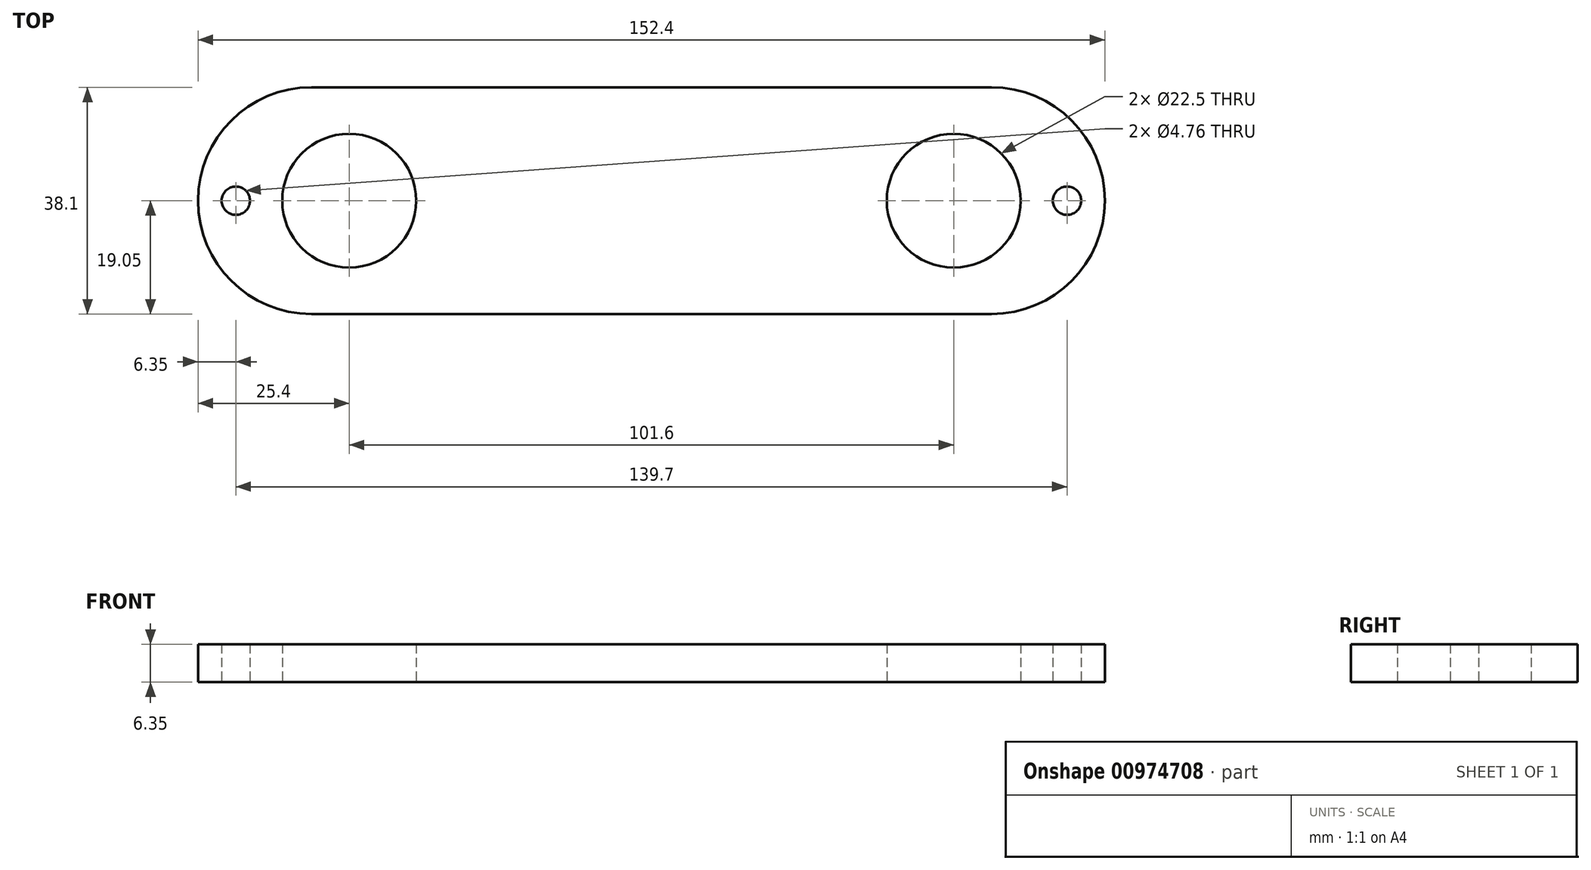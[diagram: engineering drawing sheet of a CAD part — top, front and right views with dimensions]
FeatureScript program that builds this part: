
annotation { "Feature Type Name" : "Feature", "Feature Type Description" : "" }
export const myFeature = defineFeature(function(context is Context, id is Id, definition is map)
    precondition{}
    {
        {
            var Q0;
            Q0=qCreatedBy(makeId("Top.planeOp"),FACE);
            var sketch = newSketch(context, id + "F0", { "sketchPlane" : qUnion([Q0])});
            skArc(sketch, "E0", {"start": v(-57.15, 19.05) * mm, "mid": v(-76.2, 0) * mm, "end": v(-57.15, -19.05) * mm});
            skLineSegment(sketch, "E1", {"start": v(-57.15, 19.05) * mm, "end": v(57.15, 19.05) * mm});
            skLineSegment(sketch, "E2", {"start": v(-57.15, -19.05) * mm, "end": v(57.15, -19.05) * mm});
            skArc(sketch, "E3", {"start": v(57.15, -19.05) * mm, "mid": v(76.2, 0) * mm, "end": v(57.15, 19.05) * mm});
            skCircle(sketch, "E4", {"center": v(-50.8, 0) * mm, "radius": 11.25 * mm});
            skCircle(sketch, "E5", {"center": v(50.8, 0) * mm, "radius": 11.25 * mm});
            skPoint(sketch, "E6", {"position": v(0, 0) * mm});
            skSolve(sketch);
        }
        {
            var Q0;
            Q0=makeQuery(id+"F0.imprint","IMPRINT",FACE,{"disambiguationData":[TD([[makeQuery(id+"F0.imprint","IMPRINT",EDGE,{"derivedFrom":sQuery(id+"F0.wireOp",EDGE,"E0")}),1.0]])]});
            var sketch = newSketch(context, id + "F1", { "sketchPlane" : qUnion([Q0])});
            skCircle(sketch, "E7", {"center": v(-69.85, 0) * mm, "radius": 2.38 * mm});
            skCircle(sketch, "E8", {"center": v(69.85, 0) * mm, "radius": 2.38 * mm});
            skSolve(sketch);
        }
        {
            var Q0;
            Q0 = qSketchRegion(id + "F0", true);
            extrude(context, id + "F2", {"entities" : qUnion([Q0]), "depth" : 6.35 * mm, "offsetDistance" : 25.4 * mm});
        }
        {
            var Q0;
            Q0 = qSketchRegion(id + "F1", true);
            extrude(context, id + "F3", {"entities" : qUnion([Q0]), "operationType" : NewBodyOperationType.REMOVE, "depth" : 6.35 * mm, "offsetDistance" : 25.4 * mm});
        }
    });
